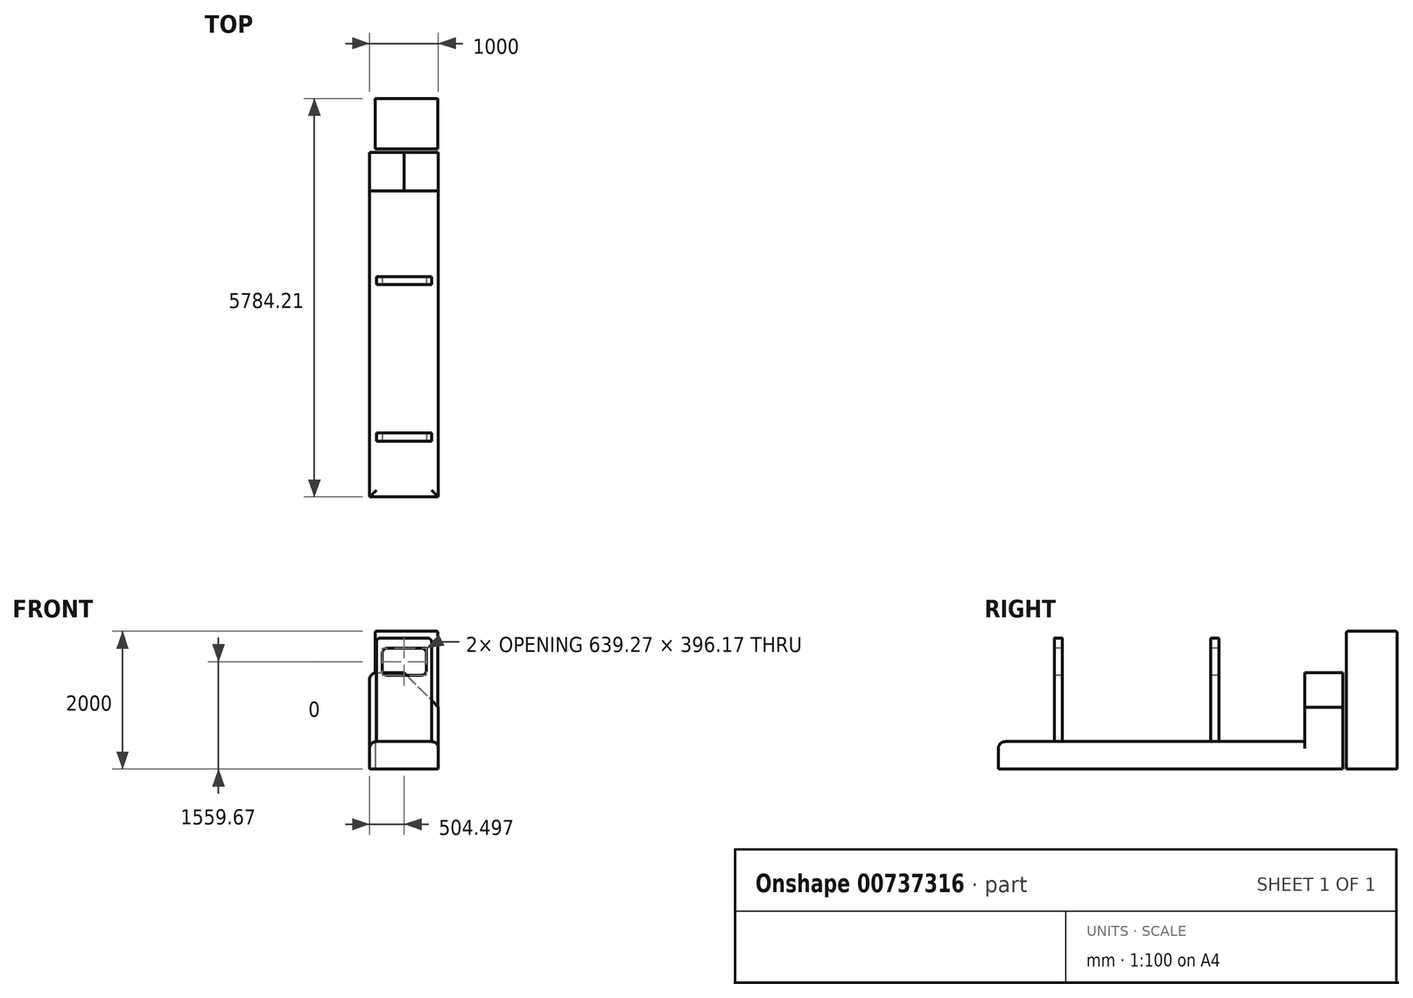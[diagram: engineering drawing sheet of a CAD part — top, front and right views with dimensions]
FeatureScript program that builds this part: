
annotation { "Feature Type Name" : "Feature", "Feature Type Description" : "" }
export const myFeature = defineFeature(function(context is Context, id is Id, definition is map)
    precondition{}
    {
        {
            var Q0;
            Q0=qCreatedBy(makeId("Front.planeOp"),FACE);
            var sketch = newSketch(context, id + "F0", { "sketchPlane" : qUnion([Q0])});
            skLineSegment(sketch, "E0.bottom", {"start": v(-495.93, 400) * mm, "end": v(504.07, 400) * mm});
            skLineSegment(sketch, "E0.top", {"start": v(-495.93, 0) * mm, "end": v(504.07, 0) * mm});
            skLineSegment(sketch, "E0.left", {"start": v(-495.93, 400) * mm, "end": v(-495.93, 0) * mm});
            skLineSegment(sketch, "E0.right", {"start": v(504.07, 400) * mm, "end": v(504.07, 0) * mm});
            skSolve(sketch);
        }
        {
            var Q0;
            Q0 = qSketchRegion(id + "F0", true);
            extrude(context, id + "F1", {"entities" : qUnion([Q0]), "depth" : 5000 * mm, "offsetDistance" : 25 * mm});
        }
        {
            var Q0;
            Q0=makeQuery(id+"F1.opExtrude","SWEPT_FACE",FACE,{"disambiguationData":[OSD([sQuery(id+"F0.wireOp",EDGE,"E0.bottom")])]});
            var sketch = newSketch(context, id + "F2", { "sketchPlane" : qUnion([Q0])});
            skLineSegment(sketch, "E1.bottom", {"start": v(-495.93, 0) * mm, "end": v(504.07, 0) * mm});
            skLineSegment(sketch, "E1.top", {"start": v(-495.93, -555.7) * mm, "end": v(504.07, -555.7) * mm});
            skLineSegment(sketch, "E1.left", {"start": v(-495.93, 0) * mm, "end": v(-495.93, -555.7) * mm});
            skLineSegment(sketch, "E1.right", {"start": v(504.07, 0) * mm, "end": v(504.07, -555.7) * mm});
            skSolve(sketch);
        }
        {
            var Q0;
            Q0 = qSketchRegion(id + "F2", true);
            extrude(context, id + "F3", {"entities" : qUnion([Q0]), "operationType" : NewBodyOperationType.ADD, "depth" : 1000 * mm, "offsetDistance" : 25 * mm});
        }
        {
            var Q0;
            Q0=makeQuery(id+"F3.opExtrude","CAP_EDGE",EDGE,{"disambiguationData":[OSD([sQuery(id+"F2.wireOp",EDGE,"E1.left")])],"isStart":false});
            var Q1;
            Q1=makeQuery(id+"F1.opExtrude","SWEPT_EDGE",EDGE,{"disambiguationData":[OSD([sQuery(id+"F0.wireOp",EDGE,"E0.bottom"),sQuery(id+"F0.wireOp",EDGE,"E0.left")])]});
            var Q2;
            Q2=makeQuery(id+"F1.opExtrude","SWEPT_EDGE",EDGE,{"disambiguationData":[OSD([sQuery(id+"F0.wireOp",EDGE,"E0.bottom"),sQuery(id+"F0.wireOp",EDGE,"E0.right")])]});
            var Q3;
            Q3=makeQuery(id+"F1.opExtrude","CAP_EDGE",EDGE,{"disambiguationData":[OSD([sQuery(id+"F0.wireOp",EDGE,"E0.bottom")])],"isStart":false});
            fillet(context, id + "F4", {"entities" : qUnion([Q0, Q1, Q2, Q3]), "radius" : 100 * mm, "tangentPropagation" : true, "defaultsChanged" : false, "vertexSettings" : [], "allowEdgeOverflow" : false});
        }
        {
            var Q0;
            Q0=makeQuery(id+"F1.opExtrude","SWEPT_FACE",FACE,{"disambiguationData":[OSD([sQuery(id+"F0.wireOp",EDGE,"E0.bottom")])]});
            var sketch = newSketch(context, id + "F5", { "sketchPlane" : qUnion([Q0])});
            skLineSegment(sketch, "E2.bottom", {"start": v(-395.93, -4070.76) * mm, "end": v(404.07, -4070.76) * mm});
            skLineSegment(sketch, "E2.top", {"start": v(-395.93, -4187.81) * mm, "end": v(404.07, -4187.81) * mm});
            skLineSegment(sketch, "E2.left", {"start": v(-395.93, -4070.76) * mm, "end": v(-395.93, -4187.81) * mm});
            skLineSegment(sketch, "E2.right", {"start": v(404.07, -4070.76) * mm, "end": v(404.07, -4187.81) * mm});
            skLineSegment(sketch, "E3.bottom", {"start": v(-395.93, -1801.81) * mm, "end": v(404.07, -1801.81) * mm});
            skLineSegment(sketch, "E3.top", {"start": v(-395.93, -1918.86) * mm, "end": v(404.07, -1918.86) * mm});
            skLineSegment(sketch, "E3.left", {"start": v(-395.93, -1801.81) * mm, "end": v(-395.93, -1918.86) * mm});
            skLineSegment(sketch, "E3.right", {"start": v(404.07, -1801.81) * mm, "end": v(404.07, -1918.86) * mm});
            skSolve(sketch);
        }
        {
            var Q0;
            Q0 = qSketchRegion(id + "F5", true);
            extrude(context, id + "F6", {"entities" : qUnion([Q0]), "operationType" : NewBodyOperationType.ADD, "depth" : 1500 * mm, "offsetDistance" : 25 * mm});
        }
        {
            var Q0;
            Q0=makeQuery(id+"F6.opExtrude","CAP_EDGE",EDGE,{"disambiguationData":[OSD([sQuery(id+"F5.wireOp",EDGE,"E2.right")])],"isStart":false});
            var Q1;
            Q1=makeQuery(id+"F6.opExtrude","CAP_EDGE",EDGE,{"disambiguationData":[OSD([sQuery(id+"F5.wireOp",EDGE,"E3.right")])],"isStart":false});
            var Q2;
            Q2=makeQuery(id+"F6.opExtrude","CAP_EDGE",EDGE,{"disambiguationData":[OSD([sQuery(id+"F5.wireOp",EDGE,"E3.left")])],"isStart":false});
            var Q3;
            Q3=makeQuery(id+"F6.opExtrude","CAP_EDGE",EDGE,{"disambiguationData":[OSD([sQuery(id+"F5.wireOp",EDGE,"E2.left")])],"isStart":false});
            fillet(context, id + "F7", {"entities" : qUnion([Q0, Q1, Q2, Q3]), "tangentPropagation" : true, "radius" : 50 * mm, "defaultsChanged" : true, "vertexSettings" : [], "allowEdgeOverflow" : false});
        }
        {
            var Q0;
            Q0=makeQuery(id+"F3.opExtrude","CAP_EDGE",EDGE,{"disambiguationData":[OSD([sQuery(id+"F2.wireOp",EDGE,"E1.right")])],"isStart":false});
            chamfer(context, id + "F8", {"entities" : qUnion([Q0]), "width" : 500 * mm, "tangentPropagation" : true});
        }
        {
            var Q0;
            Q0=makeQuery(id+"F6.opExtrude","SWEPT_FACE",FACE,{"disambiguationData":[OSD([sQuery(id+"F5.wireOp",EDGE,"E2.top")])]});
            var sketch = newSketch(context, id + "F9", { "sketchPlane" : qUnion([Q0])});
            skLineSegment(sketch, "E4.bottom", {"start": v(-311.07, 1757.75) * mm, "end": v(328.2, 1757.75) * mm});
            skLineSegment(sketch, "E4.top", {"start": v(-311.07, 1361.59) * mm, "end": v(328.2, 1361.59) * mm});
            skLineSegment(sketch, "E4.left", {"start": v(-311.07, 1757.75) * mm, "end": v(-311.07, 1361.59) * mm});
            skLineSegment(sketch, "E4.right", {"start": v(328.2, 1757.75) * mm, "end": v(328.2, 1361.59) * mm});
            skSolve(sketch);
        }
        {
            var Q0;
            Q0 = qSketchRegion(id + "F9", true);
            var Q1;
            Q1=makeQuery(id+"F6.opExtrude","SWEPT_FACE",FACE,{"disambiguationData":[OSD([sQuery(id+"F5.wireOp",EDGE,"E3.bottom")])]});
            extrude(context, id + "F10", {"entities" : qUnion([Q0]), "operationType" : NewBodyOperationType.REMOVE, "endBound" : BoundingType.UP_TO_SURFACE, "oppositeDirection" : true, "depth" : 25 * mm, "endBoundEntityFace" : qUnion([Q1]), "offsetDistance" : 25 * mm});
        }
        {
            var Q0;
            {var subQ0=sQuery(id+"F9.wireOp",EDGE,"E4.left");var subQ1=sQuery(id+"F9.wireOp",EDGE,"E4.bottom");Q0=makeQuery(id+"F10.boolean.opBoolean","COPY",EDGE,{"disambiguationData":[TD([makeQuery(id+"F6.opExtrude","SWEPT_FACE",FACE,{"disambiguationData":[OSD([sQuery(id+"F5.wireOp",EDGE,"E2.bottom")])]})])],"derivedFrom":makeQuery(id+"F10.opExtrude","SWEPT_EDGE",EDGE,{"disambiguationData":[OSD([subQ1,subQ0])]})});}
            var Q1;
            {var subQ0=sQuery(id+"F9.wireOp",EDGE,"E4.bottom");var subQ1=sQuery(id+"F9.wireOp",EDGE,"E4.left");Q1=makeQuery(id+"F10.boolean.opBoolean","COPY",EDGE,{"disambiguationData":[TD([makeQuery(id+"F6.opExtrude","SWEPT_FACE",FACE,{"disambiguationData":[OSD([sQuery(id+"F5.wireOp",EDGE,"E3.bottom")])]})])],"derivedFrom":makeQuery(id+"F10.opExtrude","SWEPT_EDGE",EDGE,{"disambiguationData":[OSD([subQ0,subQ1])]})});}
            var Q2;
            {var subQ0=sQuery(id+"F9.wireOp",EDGE,"E4.left");var subQ1=sQuery(id+"F9.wireOp",EDGE,"E4.top");Q2=makeQuery(id+"F10.boolean.opBoolean","COPY",EDGE,{"disambiguationData":[TD([makeQuery(id+"F6.opExtrude","SWEPT_FACE",FACE,{"disambiguationData":[OSD([sQuery(id+"F5.wireOp",EDGE,"E2.bottom")])]})])],"derivedFrom":makeQuery(id+"F10.opExtrude","SWEPT_EDGE",EDGE,{"disambiguationData":[OSD([subQ1,subQ0])]})});}
            var Q3;
            {var subQ0=sQuery(id+"F9.wireOp",EDGE,"E4.top");var subQ1=sQuery(id+"F9.wireOp",EDGE,"E4.left");Q3=makeQuery(id+"F10.boolean.opBoolean","COPY",EDGE,{"disambiguationData":[TD([makeQuery(id+"F6.opExtrude","SWEPT_FACE",FACE,{"disambiguationData":[OSD([sQuery(id+"F5.wireOp",EDGE,"E3.bottom")])]})])],"derivedFrom":makeQuery(id+"F10.opExtrude","SWEPT_EDGE",EDGE,{"disambiguationData":[OSD([subQ0,subQ1])]})});}
            var Q4;
            {var subQ0=sQuery(id+"F9.wireOp",EDGE,"E4.right");var subQ1=sQuery(id+"F9.wireOp",EDGE,"E4.top");Q4=makeQuery(id+"F10.boolean.opBoolean","COPY",EDGE,{"disambiguationData":[TD([makeQuery(id+"F6.opExtrude","SWEPT_FACE",FACE,{"disambiguationData":[OSD([sQuery(id+"F5.wireOp",EDGE,"E3.bottom")])]})])],"derivedFrom":makeQuery(id+"F10.opExtrude","SWEPT_EDGE",EDGE,{"disambiguationData":[OSD([subQ1,subQ0])]})});}
            var Q5;
            {var subQ0=sQuery(id+"F9.wireOp",EDGE,"E4.top");var subQ1=sQuery(id+"F9.wireOp",EDGE,"E4.right");Q5=makeQuery(id+"F10.boolean.opBoolean","COPY",EDGE,{"disambiguationData":[TD([makeQuery(id+"F6.opExtrude","SWEPT_FACE",FACE,{"disambiguationData":[OSD([sQuery(id+"F5.wireOp",EDGE,"E2.bottom")])]})])],"derivedFrom":makeQuery(id+"F10.opExtrude","SWEPT_EDGE",EDGE,{"disambiguationData":[OSD([subQ0,subQ1])]})});}
            var Q6;
            {var subQ0=sQuery(id+"F9.wireOp",EDGE,"E4.bottom");var subQ1=sQuery(id+"F9.wireOp",EDGE,"E4.right");Q6=makeQuery(id+"F10.boolean.opBoolean","COPY",EDGE,{"disambiguationData":[TD([makeQuery(id+"F6.opExtrude","SWEPT_FACE",FACE,{"disambiguationData":[OSD([sQuery(id+"F5.wireOp",EDGE,"E3.bottom")])]})])],"derivedFrom":makeQuery(id+"F10.opExtrude","SWEPT_EDGE",EDGE,{"disambiguationData":[OSD([subQ0,subQ1])]})});}
            fillet(context, id + "F11", {"entities" : qUnion([Q0, Q1, Q2, Q3, Q4, Q5, Q6]), "tangentPropagation" : true, "radius" : 75 * mm, "defaultsChanged" : false, "vertexSettings" : [], "allowEdgeOverflow" : false});
        }
        {
            var Q0;
            Q0=qCreatedBy(makeId("Top.planeOp"),FACE);
            var sketch = newSketch(context, id + "F12", { "sketchPlane" : qUnion([Q0])});
            skLineSegment(sketch, "E5.bottom", {"start": v(-416.14, 51.08) * mm, "end": v(497.27, 51.08) * mm});
            skLineSegment(sketch, "E5.top", {"start": v(-416.14, 784.21) * mm, "end": v(497.27, 784.21) * mm});
            skLineSegment(sketch, "E5.left", {"start": v(-416.14, 51.08) * mm, "end": v(-416.14, 784.21) * mm});
            skLineSegment(sketch, "E5.right", {"start": v(497.27, 51.08) * mm, "end": v(497.27, 784.21) * mm});
            skSolve(sketch);
        }
        {
            var Q0;
            Q0 = qSketchRegion(id + "F12", true);
            extrude(context, id + "F13", {"entities" : qUnion([Q0]), "depth" : 2000 * mm, "offsetDistance" : 25 * mm});
        }
        {
            var Q0;
            Q0=makeQuery(id+"F13.opExtrude","CAP_EDGE",EDGE,{"disambiguationData":[OSD([sQuery(id+"F12.wireOp",EDGE,"E5.right")])],"isStart":false});
            var Q1;
            Q1=makeQuery(id+"F13.opExtrude","SWEPT_FACE",FACE,{"disambiguationData":[OSD([sQuery(id+"F12.wireOp",EDGE,"E5.top")])]});
            var Q2;
            Q2=makeQuery(id+"F13.opExtrude","CAP_FACE",FACE,{"disambiguationData":[OSD([sQuery(id+"F12.wireOp",EDGE,"E5.bottom"),sQuery(id+"F12.wireOp",EDGE,"E5.top"),sQuery(id+"F12.wireOp",EDGE,"E5.left"),sQuery(id+"F12.wireOp",EDGE,"E5.right")])],"isStart":false});
            var Q3;
            Q3=makeQuery(id+"F13.opExtrude","SWEPT_EDGE",EDGE,{"disambiguationData":[OSD([sQuery(id+"F12.wireOp",EDGE,"E5.bottom"),sQuery(id+"F12.wireOp",EDGE,"E5.right")])]});
            fillet(context, id + "F14", {"entities" : qUnion([Q0, Q1, Q2, Q3]), "tangentPropagation" : true, "radius" : 20 * mm, "defaultsChanged" : false, "vertexSettings" : [], "allowEdgeOverflow" : false});
        }
    });
